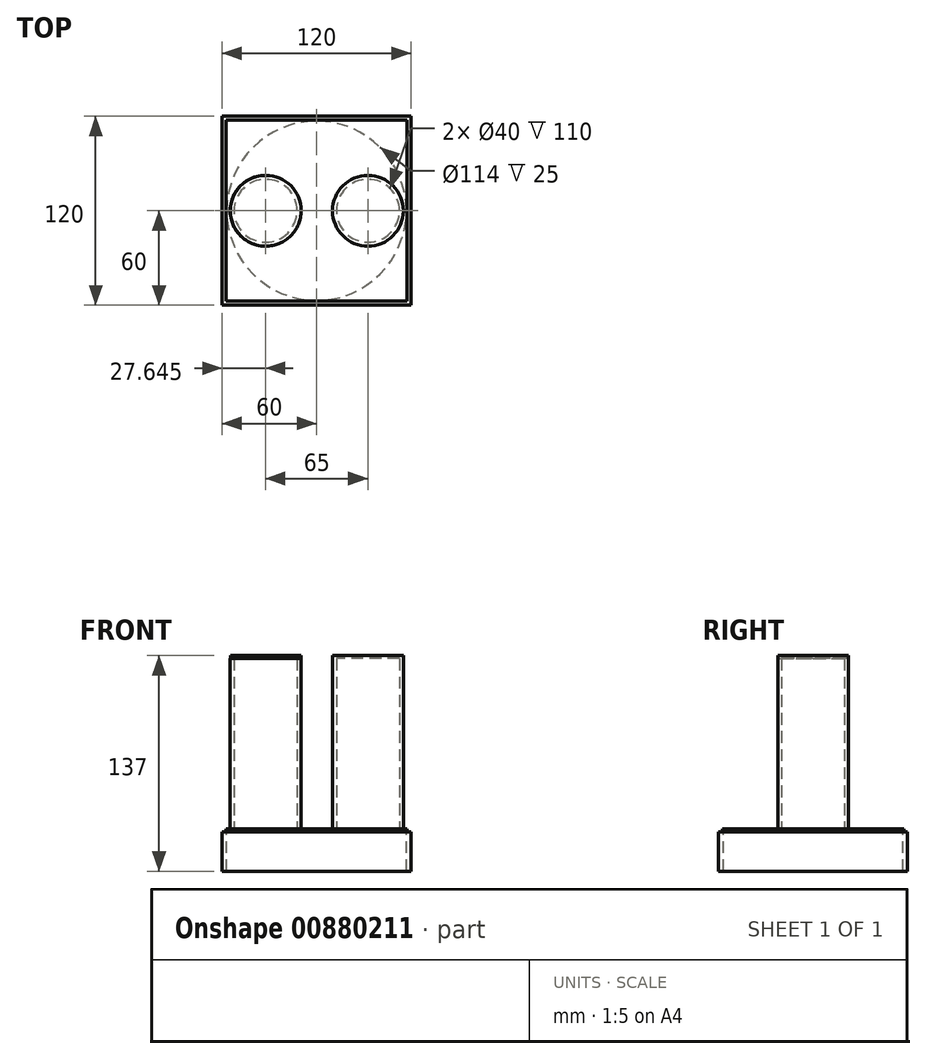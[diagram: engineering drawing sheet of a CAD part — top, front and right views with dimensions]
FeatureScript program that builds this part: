
annotation { "Feature Type Name" : "Feature", "Feature Type Description" : "" }
export const myFeature = defineFeature(function(context is Context, id is Id, definition is map)
    precondition{}
    {
        {
            var Q0;
            Q0=qCreatedBy(makeId("Top.planeOp"),FACE);
            var sketch = newSketch(context, id + "F0", { "sketchPlane" : qUnion([Q0])});
            skLineSegment(sketch, "E0.bottom", {"start": v(60, -60) * mm, "end": v(-60, -60) * mm});
            skLineSegment(sketch, "E0.top", {"start": v(60, 60) * mm, "end": v(-60, 60) * mm});
            skLineSegment(sketch, "E0.left", {"start": v(60, -60) * mm, "end": v(60, 60) * mm});
            skLineSegment(sketch, "E0.right", {"start": v(-60, -60) * mm, "end": v(-60, 60) * mm});
            skPoint(sketch, "E0.middle", {"position": v(0, 0) * mm});
            skCircle(sketch, "E1", {"center": v(0, 0) * mm, "radius": 57 * mm});
            skSolve(sketch);
        }
        {
            var Q0;
            Q0=makeQuery(id+"F0.imprint","IMPRINT",FACE,{"disambiguationData":[TD([[makeQuery(id+"F0.imprint","IMPRINT",EDGE,{"derivedFrom":sQuery(id+"F0.wireOp",EDGE,"E0.bottom")}),-1.0]])]});
            extrude(context, id + "F1", {"entities" : qUnion([Q0]), "oppositeDirection" : true, "depth" : 25 * mm, "offsetDistance" : 25 * mm});
        }
        {
            var Q0;
            Q0=qCreatedBy(makeId("Top.planeOp"),FACE);
            var sketch = newSketch(context, id + "F2", { "sketchPlane" : qUnion([Q0])});
            skLineSegment(sketch, "E2", {"start": v(0, 0) * mm, "end": v(-64.7, 0) * mm, "construction": true});
            skCircle(sketch, "E3", {"center": v(-32.35, 0) * mm, "radius": 22.5 * mm});
            skLineSegment(sketch, "E4", {"start": v(0, 0) * mm, "end": v(65.3, 0) * mm, "construction": true});
            skCircle(sketch, "E5", {"center": v(32.65, 0) * mm, "radius": 22.5 * mm});
            skLineSegment(sketch, "E6.bottom", {"start": v(57.5, -57.5) * mm, "end": v(-57.5, -57.5) * mm});
            skLineSegment(sketch, "E6.top", {"start": v(57.5, 57.5) * mm, "end": v(-57.5, 57.5) * mm});
            skLineSegment(sketch, "E6.left", {"start": v(57.5, -57.5) * mm, "end": v(57.5, 57.5) * mm});
            skLineSegment(sketch, "E6.right", {"start": v(-57.5, -57.5) * mm, "end": v(-57.5, 57.5) * mm});
            skPoint(sketch, "E6.middle", {"position": v(0, 0) * mm});
            skCircle(sketch, "E7", {"center": v(-32.35, 0) * mm, "radius": 20 * mm});
            skCircle(sketch, "E8", {"center": v(32.65, 0) * mm, "radius": 20 * mm});
            skSolve(sketch);
        }
        {
            var Q0;
            Q0=makeQuery(id+"F2.imprint","IMPRINT",FACE,{"disambiguationData":[TD([[makeQuery(id+"F2.imprint","IMPRINT",EDGE,{"derivedFrom":sQuery(id+"F2.wireOp",EDGE,"E3")}),-1.0]])]});
            extrude(context, id + "F3", {"entities" : qUnion([Q0]), "operationType" : NewBodyOperationType.ADD, "depth" : 2 * mm, "offsetDistance" : 25 * mm});
        }
        {
            var Q0;
            Q0=makeQuery(id+"F2.imprint","IMPRINT",FACE,{"disambiguationData":[TD([[makeQuery(id+"F2.imprint","IMPRINT",EDGE,{"derivedFrom":sQuery(id+"F2.wireOp",EDGE,"E3")}),1.0]])]});
            var Q1;
            Q1=makeQuery(id+"F2.imprint","IMPRINT",FACE,{"disambiguationData":[TD([[makeQuery(id+"F2.imprint","IMPRINT",EDGE,{"derivedFrom":sQuery(id+"F2.wireOp",EDGE,"E5")}),1.0]])]});
            extrude(context, id + "F4", {"entities" : qUnion([Q0, Q1]), "operationType" : NewBodyOperationType.ADD, "depth" : 110 * mm, "offsetDistance" : 25 * mm});
        }
        {
            var Q0;
            Q0=makeQuery(id+"F4.opExtrude","CAP_FACE",FACE,{"disambiguationData":[OSD([sQuery(id+"F2.wireOp",EDGE,"E5"),sQuery(id+"F2.wireOp",EDGE,"E8")])],"isStart":false});
            var sketch = newSketch(context, id + "F5", { "sketchPlane" : qUnion([Q0])});
            skCircle(sketch, "E9", {"center": v(-32.25, 0) * mm, "radius": 22.5 * mm});
            skCircle(sketch, "E10", {"center": v(32.65, 0) * mm, "radius": 22.5 * mm});
            skSolve(sketch);
        }
        {
            var Q0;
            Q0=makeQuery(id+"F5.imprint","IMPRINT",FACE,{"disambiguationData":[TD([[makeQuery(id+"F5.imprint","IMPRINT",EDGE,{"derivedFrom":sQuery(id+"F5.wireOp",EDGE,"E9")}),1.0]])]});
            var Q1;
            Q1=makeQuery(id+"F5.imprint","IMPRINT",FACE,{"disambiguationData":[TD([[makeQuery(id+"F5.imprint","IMPRINT",EDGE,{"derivedFrom":makeQuery(id+"F4.opExtrude","CAP_EDGE",EDGE,{"disambiguationData":[OSD([sQuery(id+"F2.wireOp",EDGE,"E8")])],"isStart":false})}),1.0]])]});
            var Q2;
            Q2=makeQuery(id+"F5.imprint","IMPRINT",FACE,{"disambiguationData":[TD([[makeQuery(id+"F5.imprint","IMPRINT",EDGE,{"derivedFrom":sQuery(id+"F5.wireOp",EDGE,"E10")}),1.0]])]});
            extrude(context, id + "F6", {"entities" : qUnion([Q0, Q1, Q2]), "operationType" : NewBodyOperationType.ADD, "depth" : 2 * mm, "offsetDistance" : 25 * mm});
        }
    });
